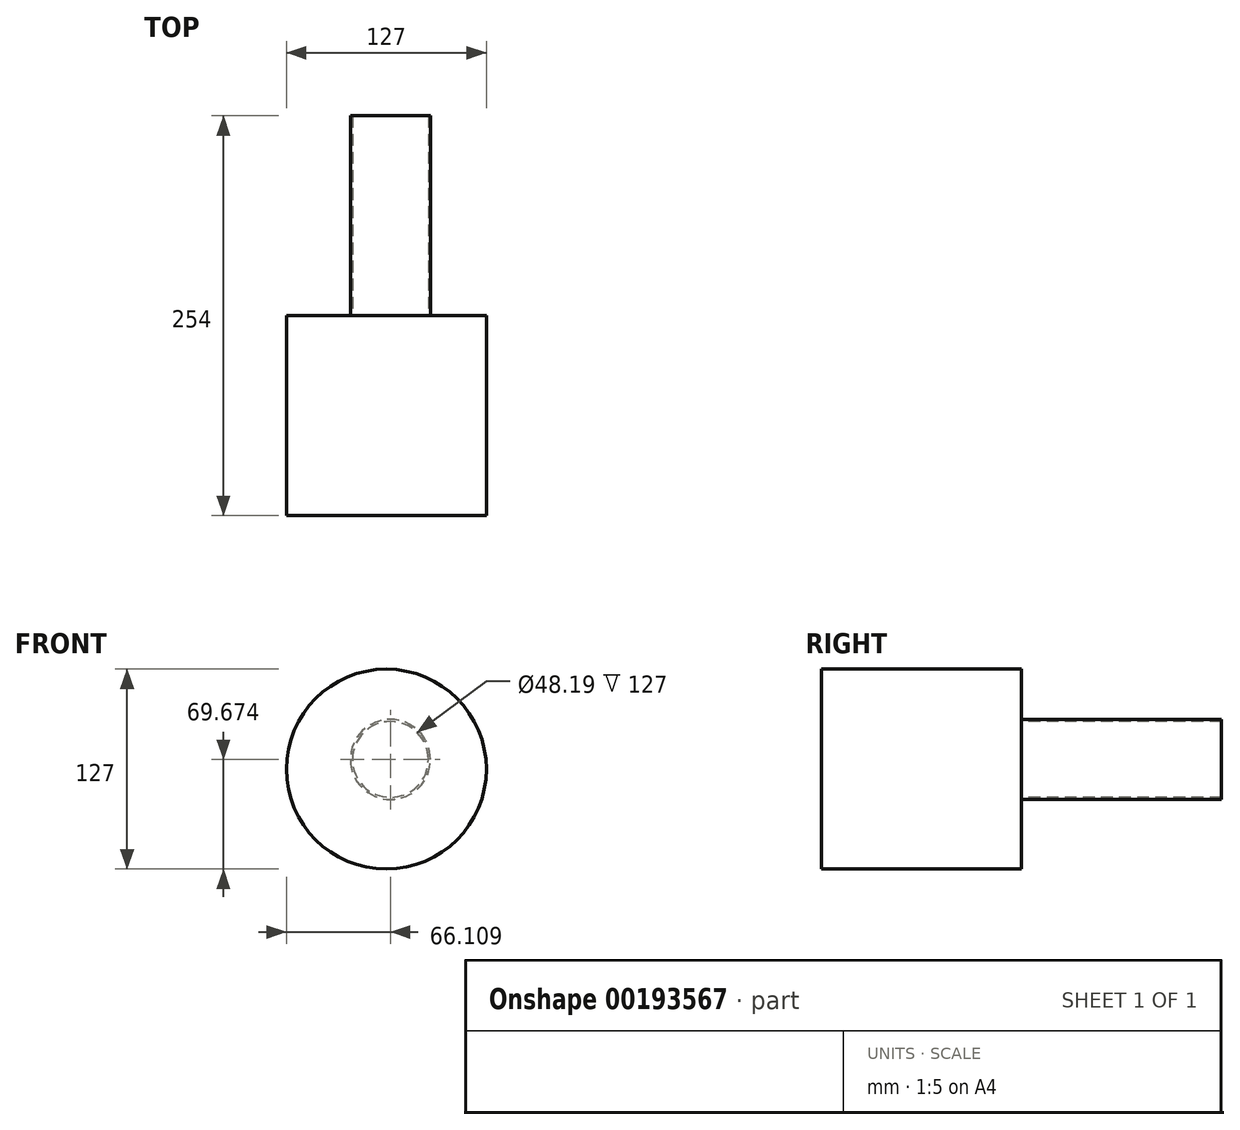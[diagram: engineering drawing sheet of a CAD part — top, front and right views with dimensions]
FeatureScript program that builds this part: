
annotation { "Feature Type Name" : "Feature", "Feature Type Description" : "" }
export const myFeature = defineFeature(function(context is Context, id is Id, definition is map)
    precondition{}
    {
        {
            var Q0;
            Q0=qCreatedBy(makeId("Front.planeOp"),FACE);
            var sketch = newSketch(context, id + "F0", { "sketchPlane" : qUnion([Q0])});
            skCircle(sketch, "E0", {"center": v(-63.63, 65.61) * mm, "radius": 63.5 * mm});
            skSolve(sketch);
        }
        {
            var Q0;
            Q0 = qSketchRegion(id + "F0", true);
            extrude(context, id + "F1", {"entities" : qUnion([Q0]), "depth" : 127 * mm});
        }
        {
            var Q0;
            Q0=makeQuery(id+"F1.opExtrude","CAP_FACE",FACE,{"disambiguationData":[OSD([sQuery(id+"F0.wireOp",EDGE,"E0")])],"isStart":true});
            var sketch = newSketch(context, id + "F2", { "sketchPlane" : qUnion([Q0])});
            skCircle(sketch, "E1", {"center": v(61.02, 71.78) * mm, "radius": 24.1 * mm});
            skCircle(sketch, "E2", {"center": v(61.02, 71.78) * mm, "radius": 25.4 * mm});
            skSolve(sketch);
        }
        {
            var Q0;
            Q0 = qSketchRegion(id + "F2", true);
            extrude(context, id + "F3", {"entities" : qUnion([Q0]), "operationType" : NewBodyOperationType.ADD, "depth" : 127 * mm});
        }
    });
